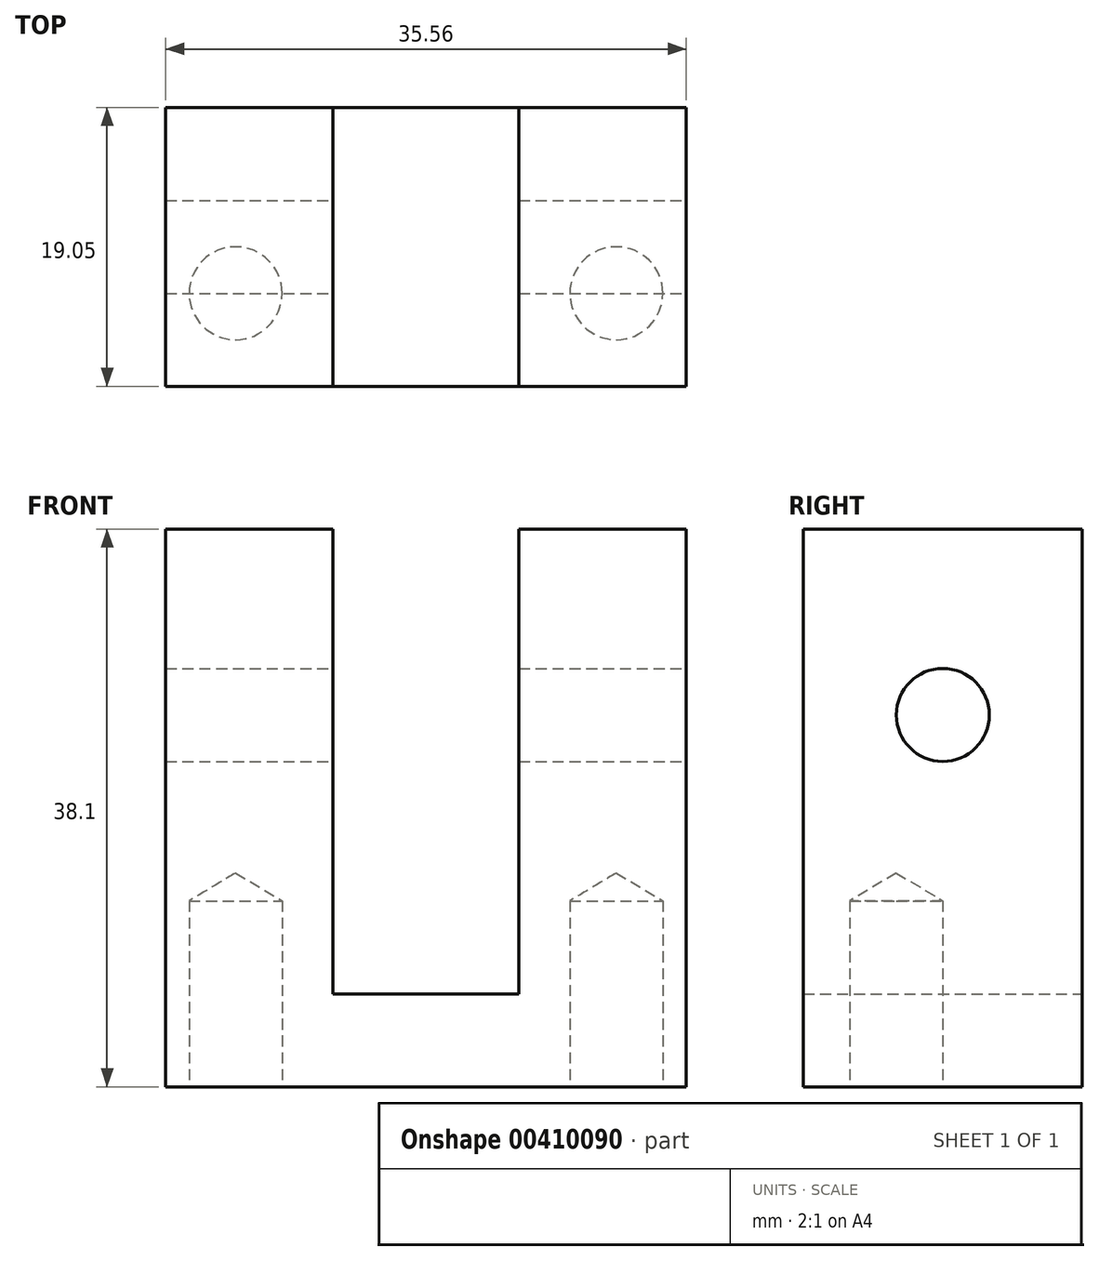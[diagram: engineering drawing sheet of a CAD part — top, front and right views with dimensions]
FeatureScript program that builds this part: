
annotation { "Feature Type Name" : "Feature", "Feature Type Description" : "" }
export const myFeature = defineFeature(function(context is Context, id is Id, definition is map)
    precondition{}
    {
        {
            var Q0;
            Q0=qCreatedBy(makeId("Front.planeOp"),FACE);
            var sketch = newSketch(context, id + "F0", { "sketchPlane" : qUnion([Q0])});
            skLineSegment(sketch, "E0.bottom", {"start": v(-17.78, 38.1) * mm, "end": v(-6.35, 38.1) * mm});
            skLineSegment(sketch, "E0.top", {"start": v(-17.78, 0) * mm, "end": v(17.78, 0) * mm});
            skLineSegment(sketch, "E0.left", {"start": v(-17.78, 38.1) * mm, "end": v(-17.78, 0) * mm});
            skLineSegment(sketch, "E0.right", {"start": v(17.78, 38.1) * mm, "end": v(17.78, 0) * mm});
            skLineSegment(sketch, "E1.top", {"start": v(-6.35, 6.35) * mm, "end": v(6.35, 6.35) * mm});
            skLineSegment(sketch, "E1.left", {"start": v(-6.35, 38.1) * mm, "end": v(-6.35, 6.35) * mm});
            skLineSegment(sketch, "E1.right", {"start": v(6.35, 38.1) * mm, "end": v(6.35, 6.35) * mm});
            skLineSegment(sketch, "E2.trimOffspring", {"start": v(6.35, 38.1) * mm, "end": v(17.78, 38.1) * mm});
            skSolve(sketch);
        }
        {
            var Q0;
            Q0=makeQuery(id+"F0.imprint","IMPRINT",FACE,{"disambiguationData":[TD([[makeQuery(id+"F0.imprint","IMPRINT",EDGE,{"derivedFrom":sQuery(id+"F0.wireOp",EDGE,"E0.bottom")}),-1.0]])]});
            extrude(context, id + "F1", {"entities" : qUnion([Q0]), "depth" : 19.05 * mm});
        }
        {
            var Q0;
            Q0=makeQuery(id+"F1.opExtrude","SWEPT_FACE",FACE,{"disambiguationData":[OSD([sQuery(id+"F0.wireOp",EDGE,"E0.right")])]});
            var sketch = newSketch(context, id + "F2", { "sketchPlane" : qUnion([Q0])});
            skLineSegment(sketch, "E3.0.0", {"start": v(0, 0) * mm, "end": v(0, 38.1) * mm});
            skLineSegment(sketch, "E3.0.1", {"start": v(0, 38.1) * mm, "end": v(-19.05, 38.1) * mm});
            skLineSegment(sketch, "E3.0.2", {"start": v(-19.05, 38.1) * mm, "end": v(-19.05, 0) * mm});
            skLineSegment(sketch, "E3.0.3", {"start": v(-19.05, 0) * mm, "end": v(0, 0) * mm});
            skCircle(sketch, "E4", {"center": v(-9.52, 25.4) * mm, "radius": 3.18 * mm});
            skSolve(sketch);
        }
        {
            var Q0;
            Q0=makeQuery(id+"F2.imprint","IMPRINT",FACE,{"disambiguationData":[TD([[makeQuery(id+"F2.imprint","IMPRINT",EDGE,{"derivedFrom":sQuery(id+"F2.wireOp",EDGE,"E4")}),1.0]])]});
            extrude(context, id + "F3", {"entities" : qUnion([Q0]), "operationType" : NewBodyOperationType.REMOVE, "endBound" : BoundingType.THROUGH_ALL, "oppositeDirection" : true, "depth" : 25.4 * mm});
        }
        {
            var Q0;
            Q0=makeQuery(id+"F1.opExtrude","SWEPT_FACE",FACE,{"disambiguationData":[OSD([sQuery(id+"F0.wireOp",EDGE,"E0.top")])]});
            var sketch = newSketch(context, id + "F4", { "sketchPlane" : qUnion([Q0])});
            skPoint(sketch, "E5", {"position": v(-13, 12.7) * mm});
            skPoint(sketch, "E6", {"position": v(13, 12.7) * mm});
            skSolve(sketch);
        }
        {
            var Q0;
            Q0=sQuery(id+"F4.wireOp",VERTEX,"E5");
            var Q1;
            Q1=sQuery(id+"F4.wireOp",VERTEX,"E6");
            var Q2;
            Q2=makeQuery(id+"F1.opExtrude","SWEPT_BODY",BODY,{"disambiguationData":[OSD([sQuery(id+"F0.wireOp",EDGE,"E0.bottom"),sQuery(id+"F0.wireOp",EDGE,"E0.top"),sQuery(id+"F0.wireOp",EDGE,"E0.left"),sQuery(id+"F0.wireOp",EDGE,"E0.right"),sQuery(id+"F0.wireOp",EDGE,"E1.top"),sQuery(id+"F0.wireOp",EDGE,"E1.left"),sQuery(id+"F0.wireOp",EDGE,"E1.right"),sQuery(id+"F0.wireOp",EDGE,"E2.trimOffspring")])]});
            hole(context, id + "F5", {"style" : HoleStyle.SIMPLE, "endStyle" : HoleEndStyle.BLIND, "holeDiameter" : 6.35 * mm, "holeDepth" : 12.7 * mm, "isTappedThrough" : true, "tappedDepth" : 12.7 * mm, "tapClearance" : 3, "locations" : qUnion([Q0, Q1]), "scope" : qUnion([Q2])});
        }
    });
